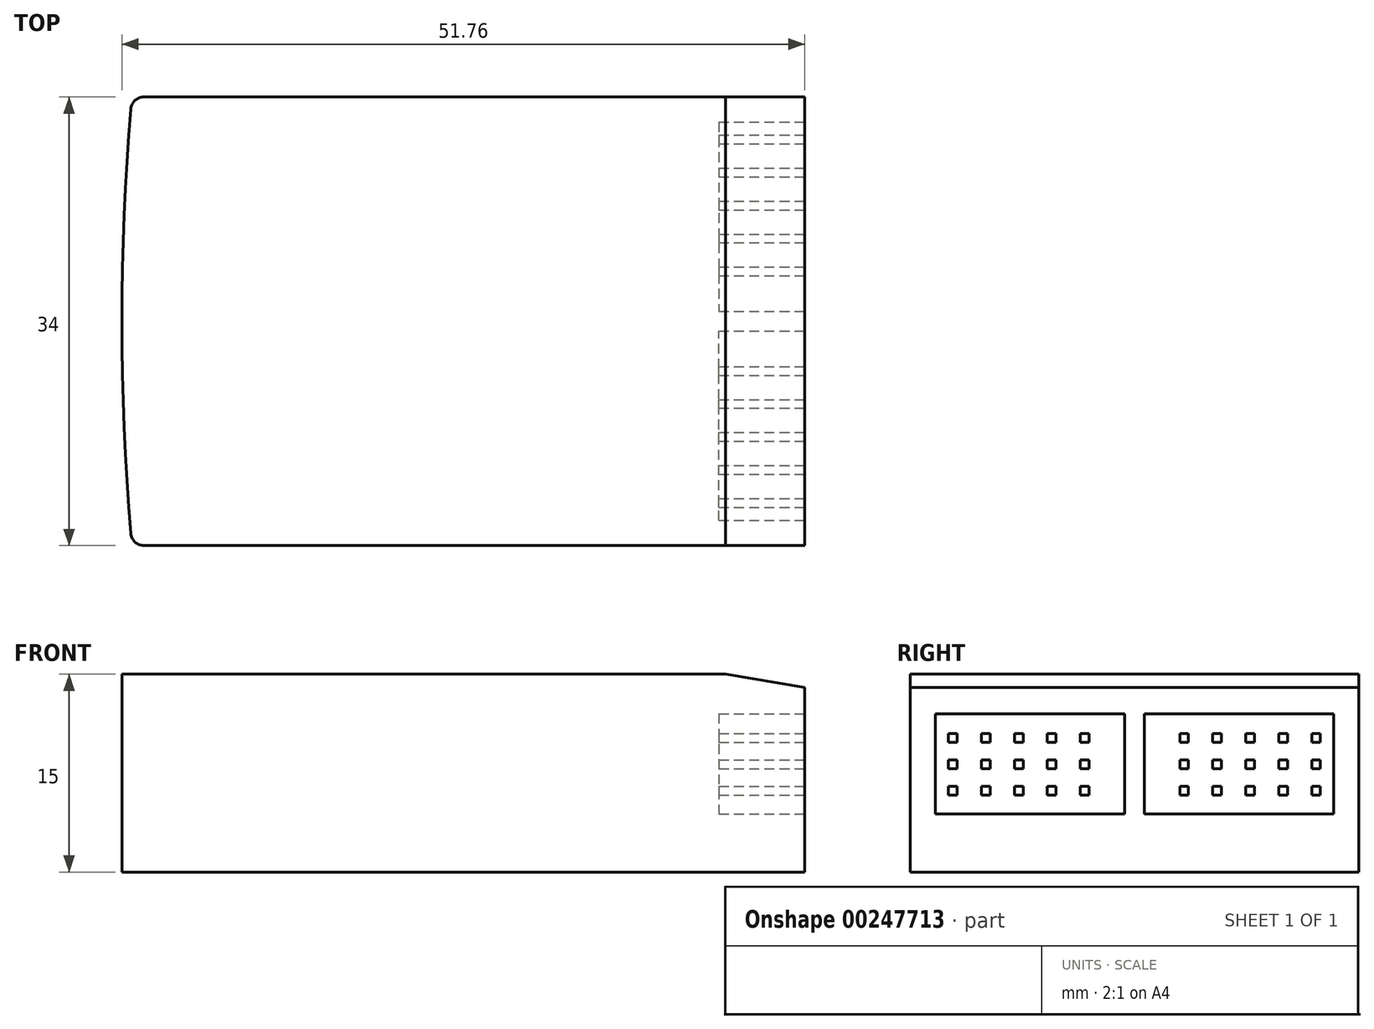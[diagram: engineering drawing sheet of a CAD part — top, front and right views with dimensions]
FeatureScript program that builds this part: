
annotation { "Feature Type Name" : "Feature", "Feature Type Description" : "" }
export const myFeature = defineFeature(function(context is Context, id is Id, definition is map)
    precondition{}
    {
        {
            var Q0;
            Q0=qCreatedBy(makeId("Top.planeOp"),FACE);
            var sketch = newSketch(context, id + "F0", { "sketchPlane" : qUnion([Q0])});
            skLineSegment(sketch, "E0.bottom", {"start": v(-8.7, 28.02) * mm, "end": v(42.3, 28.02) * mm});
            skLineSegment(sketch, "E0.top", {"start": v(-8.7, -5.98) * mm, "end": v(42.3, -5.98) * mm});
            skLineSegment(sketch, "E0.right", {"start": v(42.3, 28.02) * mm, "end": v(42.3, -5.98) * mm});
            skArc(sketch, "E1", {"start": v(-8.7, 28.02) * mm, "mid": v(-9.46, 11.02) * mm, "end": v(-8.7, -5.98) * mm});
            skSolve(sketch);
        }
        {
            var Q0;
            Q0 = qSketchRegion(id + "F0", true);
            extrude(context, id + "F1", {"entities" : qUnion([Q0]), "depth" : 15 * mm});
        }
        {
            var Q0;
            Q0=makeQuery(id+"F1.opExtrude","CAP_EDGE",EDGE,{"disambiguationData":[OSD([sQuery(id+"F0.wireOp",EDGE,"E0.right")])],"isStart":false});
            chamfer(context, id + "F2", {"entities" : qUnion([Q0]), "chamferType" : ChamferType.TWO_OFFSETS, "width1" : 1 * mm, "oppositeDirection" : false, "width2" : 6 * mm, "tangentPropagation" : true});
        }
        {
            var Q0;
            Q0=makeQuery(id+"F1.opExtrude","SWEPT_FACE",FACE,{"disambiguationData":[OSD([sQuery(id+"F0.wireOp",EDGE,"E0.right")])]});
            var sketch = newSketch(context, id + "F3", { "sketchPlane" : qUnion([Q0])});
            skLineSegment(sketch, "E2", {"start": v(11.02, 14) * mm, "end": v(11.02, 0) * mm});
            skLineSegment(sketch, "E3.bottom", {"start": v(-4.08, 12) * mm, "end": v(9.92, 12) * mm});
            skLineSegment(sketch, "E3.top", {"start": v(-4.08, 4.4) * mm, "end": v(9.92, 4.4) * mm});
            skLineSegment(sketch, "E3.left", {"start": v(-4.08, 12) * mm, "end": v(-4.08, 4.4) * mm});
            skLineSegment(sketch, "E4", {"start": v(10.27, 14) * mm, "end": v(10.27, 0) * mm});
            skLineSegment(sketch, "E5.MirrorCS", {"start": v(11.77, 14) * mm, "end": v(11.77, 0) * mm});
            skLineSegment(sketch, "E6.0", {"start": v(28.02, 14) * mm, "end": v(28.02, 0) * mm});
            skLineSegment(sketch, "E7", {"start": v(9.92, 4.4) * mm, "end": v(10.27, 4.4) * mm});
            skLineSegment(sketch, "E8", {"start": v(9.92, 12) * mm, "end": v(10.27, 12) * mm});
            skLineSegment(sketch, "E9.MirrorCS", {"start": v(12.12, 4.4) * mm, "end": v(11.77, 4.4) * mm});
            skLineSegment(sketch, "E10.MirrorCS", {"start": v(12.12, 12) * mm, "end": v(11.77, 12) * mm});
            skLineSegment(sketch, "E11.MirrorCS", {"start": v(26.12, 12) * mm, "end": v(12.12, 12) * mm});
            skLineSegment(sketch, "E12.MirrorCS", {"start": v(26.12, 12) * mm, "end": v(26.12, 4.4) * mm});
            skLineSegment(sketch, "E13.MirrorCS", {"start": v(26.12, 4.4) * mm, "end": v(12.12, 4.4) * mm});
            skLineSegment(sketch, "E14.bottom", {"start": v(-3.08, 10.5) * mm, "end": v(-2.42, 10.5) * mm});
            skLineSegment(sketch, "E14.top", {"start": v(-3.08, 9.84) * mm, "end": v(-2.42, 9.84) * mm});
            skLineSegment(sketch, "E14.left", {"start": v(-3.08, 10.5) * mm, "end": v(-3.08, 9.84) * mm});
            skLineSegment(sketch, "E14.right", {"start": v(-2.42, 10.5) * mm, "end": v(-2.42, 9.84) * mm});
            skLineSegment(sketch, "E15.0.1.0", {"start": v(-2.42, 8.5) * mm, "end": v(-2.42, 7.84) * mm});
            skLineSegment(sketch, "E15.0.1.1", {"start": v(-3.08, 8.5) * mm, "end": v(-2.42, 8.5) * mm});
            skLineSegment(sketch, "E15.0.1.2", {"start": v(-3.08, 8.5) * mm, "end": v(-3.08, 7.84) * mm});
            skLineSegment(sketch, "E15.0.1.3", {"start": v(-3.08, 7.84) * mm, "end": v(-2.42, 7.84) * mm});
            skLineSegment(sketch, "E15.0.2.0", {"start": v(-2.42, 6.5) * mm, "end": v(-2.42, 5.84) * mm});
            skLineSegment(sketch, "E15.0.2.1", {"start": v(-3.08, 6.5) * mm, "end": v(-2.42, 6.5) * mm});
            skLineSegment(sketch, "E15.0.2.2", {"start": v(-3.08, 6.5) * mm, "end": v(-3.08, 5.84) * mm});
            skLineSegment(sketch, "E15.0.2.3", {"start": v(-3.08, 5.84) * mm, "end": v(-2.42, 5.84) * mm});
            skLineSegment(sketch, "E15.1.0.0", {"start": v(0.08, 10.5) * mm, "end": v(0.08, 9.84) * mm});
            skLineSegment(sketch, "E15.1.0.1", {"start": v(-0.58, 10.5) * mm, "end": v(0.08, 10.5) * mm});
            skLineSegment(sketch, "E15.1.0.2", {"start": v(-0.58, 10.5) * mm, "end": v(-0.58, 9.84) * mm});
            skLineSegment(sketch, "E15.1.0.3", {"start": v(-0.58, 9.84) * mm, "end": v(0.08, 9.84) * mm});
            skLineSegment(sketch, "E15.1.1.0", {"start": v(0.08, 8.5) * mm, "end": v(0.08, 7.84) * mm});
            skLineSegment(sketch, "E15.1.1.1", {"start": v(-0.58, 8.5) * mm, "end": v(0.08, 8.5) * mm});
            skLineSegment(sketch, "E15.1.1.2", {"start": v(-0.58, 8.5) * mm, "end": v(-0.58, 7.84) * mm});
            skLineSegment(sketch, "E15.1.1.3", {"start": v(-0.58, 7.84) * mm, "end": v(0.08, 7.84) * mm});
            skLineSegment(sketch, "E15.1.2.0", {"start": v(0.08, 6.5) * mm, "end": v(0.08, 5.84) * mm});
            skLineSegment(sketch, "E15.1.2.1", {"start": v(-0.58, 6.5) * mm, "end": v(0.08, 6.5) * mm});
            skLineSegment(sketch, "E15.1.2.2", {"start": v(-0.58, 6.5) * mm, "end": v(-0.58, 5.84) * mm});
            skLineSegment(sketch, "E15.1.2.3", {"start": v(-0.58, 5.84) * mm, "end": v(0.08, 5.84) * mm});
            skLineSegment(sketch, "E15.2.0.0", {"start": v(2.58, 10.5) * mm, "end": v(2.58, 9.84) * mm});
            skLineSegment(sketch, "E15.2.0.1", {"start": v(1.92, 10.5) * mm, "end": v(2.58, 10.5) * mm});
            skLineSegment(sketch, "E15.2.0.2", {"start": v(1.92, 10.5) * mm, "end": v(1.92, 9.84) * mm});
            skLineSegment(sketch, "E15.2.0.3", {"start": v(1.92, 9.84) * mm, "end": v(2.58, 9.84) * mm});
            skLineSegment(sketch, "E15.2.1.0", {"start": v(2.58, 8.5) * mm, "end": v(2.58, 7.84) * mm});
            skLineSegment(sketch, "E15.2.1.1", {"start": v(1.92, 8.5) * mm, "end": v(2.58, 8.5) * mm});
            skLineSegment(sketch, "E15.2.1.2", {"start": v(1.92, 8.5) * mm, "end": v(1.92, 7.84) * mm});
            skLineSegment(sketch, "E15.2.1.3", {"start": v(1.92, 7.84) * mm, "end": v(2.58, 7.84) * mm});
            skLineSegment(sketch, "E15.2.2.0", {"start": v(2.58, 6.5) * mm, "end": v(2.58, 5.84) * mm});
            skLineSegment(sketch, "E15.2.2.1", {"start": v(1.92, 6.5) * mm, "end": v(2.58, 6.5) * mm});
            skLineSegment(sketch, "E15.2.2.2", {"start": v(1.92, 6.5) * mm, "end": v(1.92, 5.84) * mm});
            skLineSegment(sketch, "E15.2.2.3", {"start": v(1.92, 5.84) * mm, "end": v(2.58, 5.84) * mm});
            skLineSegment(sketch, "E15.3.0.0", {"start": v(5.08, 10.5) * mm, "end": v(5.08, 9.84) * mm});
            skLineSegment(sketch, "E15.3.0.1", {"start": v(4.42, 10.5) * mm, "end": v(5.08, 10.5) * mm});
            skLineSegment(sketch, "E15.3.0.2", {"start": v(4.42, 10.5) * mm, "end": v(4.42, 9.84) * mm});
            skLineSegment(sketch, "E15.3.0.3", {"start": v(4.42, 9.84) * mm, "end": v(5.08, 9.84) * mm});
            skLineSegment(sketch, "E15.3.1.0", {"start": v(5.08, 8.5) * mm, "end": v(5.08, 7.84) * mm});
            skLineSegment(sketch, "E15.3.1.1", {"start": v(4.42, 8.5) * mm, "end": v(5.08, 8.5) * mm});
            skLineSegment(sketch, "E15.3.1.2", {"start": v(4.42, 8.5) * mm, "end": v(4.42, 7.84) * mm});
            skLineSegment(sketch, "E15.3.1.3", {"start": v(4.42, 7.84) * mm, "end": v(5.08, 7.84) * mm});
            skLineSegment(sketch, "E15.3.2.0", {"start": v(5.08, 6.5) * mm, "end": v(5.08, 5.84) * mm});
            skLineSegment(sketch, "E15.3.2.1", {"start": v(4.42, 6.5) * mm, "end": v(5.08, 6.5) * mm});
            skLineSegment(sketch, "E15.3.2.2", {"start": v(4.42, 6.5) * mm, "end": v(4.42, 5.84) * mm});
            skLineSegment(sketch, "E15.3.2.3", {"start": v(4.42, 5.84) * mm, "end": v(5.08, 5.84) * mm});
            skLineSegment(sketch, "E15.4.0.0", {"start": v(7.58, 10.5) * mm, "end": v(7.58, 9.84) * mm});
            skLineSegment(sketch, "E15.4.0.1", {"start": v(6.92, 10.5) * mm, "end": v(7.58, 10.5) * mm});
            skLineSegment(sketch, "E15.4.0.2", {"start": v(6.92, 10.5) * mm, "end": v(6.92, 9.84) * mm});
            skLineSegment(sketch, "E15.4.0.3", {"start": v(6.92, 9.84) * mm, "end": v(7.58, 9.84) * mm});
            skLineSegment(sketch, "E15.4.1.0", {"start": v(7.58, 8.5) * mm, "end": v(7.58, 7.84) * mm});
            skLineSegment(sketch, "E15.4.1.1", {"start": v(6.92, 8.5) * mm, "end": v(7.58, 8.5) * mm});
            skLineSegment(sketch, "E15.4.1.2", {"start": v(6.92, 8.5) * mm, "end": v(6.92, 7.84) * mm});
            skLineSegment(sketch, "E15.4.1.3", {"start": v(6.92, 7.84) * mm, "end": v(7.58, 7.84) * mm});
            skLineSegment(sketch, "E15.4.2.0", {"start": v(7.58, 6.5) * mm, "end": v(7.58, 5.84) * mm});
            skLineSegment(sketch, "E15.4.2.1", {"start": v(6.92, 6.5) * mm, "end": v(7.58, 6.5) * mm});
            skLineSegment(sketch, "E15.4.2.2", {"start": v(6.92, 6.5) * mm, "end": v(6.92, 5.84) * mm});
            skLineSegment(sketch, "E15.4.2.3", {"start": v(6.92, 5.84) * mm, "end": v(7.58, 5.84) * mm});
            skLineSegment(sketch, "E15.direction1", {"start": v(-3.08, 9.84) * mm, "end": v(-0.58, 9.84) * mm, "construction": true});
            skLineSegment(sketch, "E15.direction2", {"start": v(-3.08, 9.84) * mm, "end": v(-3.08, 7.84) * mm, "construction": true});
            skLineSegment(sketch, "E16.MirrorCS", {"start": v(25.12, 9.84) * mm, "end": v(24.46, 9.84) * mm});
            skLineSegment(sketch, "E17.MirrorCS", {"start": v(25.12, 8.5) * mm, "end": v(25.12, 7.84) * mm});
            skLineSegment(sketch, "E18.MirrorCS", {"start": v(17.62, 6.5) * mm, "end": v(17.62, 5.84) * mm});
            skLineSegment(sketch, "E19.MirrorCS", {"start": v(20.12, 8.5) * mm, "end": v(20.12, 7.84) * mm});
            skLineSegment(sketch, "E20.MirrorCS", {"start": v(22.62, 10.5) * mm, "end": v(22.62, 9.84) * mm});
            skLineSegment(sketch, "E21.MirrorCS", {"start": v(25.12, 7.84) * mm, "end": v(24.46, 7.84) * mm});
            skLineSegment(sketch, "E22.MirrorCS", {"start": v(14.46, 10.5) * mm, "end": v(14.46, 9.84) * mm});
            skLineSegment(sketch, "E23.MirrorCS", {"start": v(15.12, 7.84) * mm, "end": v(14.46, 7.84) * mm});
            skLineSegment(sketch, "E24.MirrorCS", {"start": v(17.62, 9.84) * mm, "end": v(16.96, 9.84) * mm});
            skLineSegment(sketch, "E25.MirrorCS", {"start": v(19.46, 6.5) * mm, "end": v(19.46, 5.84) * mm});
            skLineSegment(sketch, "E26.MirrorCS", {"start": v(22.62, 5.84) * mm, "end": v(21.96, 5.84) * mm});
            skLineSegment(sketch, "E27.MirrorCS", {"start": v(21.96, 8.5) * mm, "end": v(21.96, 7.84) * mm});
            skLineSegment(sketch, "E28.MirrorCS", {"start": v(24.46, 6.5) * mm, "end": v(24.46, 5.84) * mm});
            skLineSegment(sketch, "E29.MirrorCS", {"start": v(15.12, 10.5) * mm, "end": v(14.46, 10.5) * mm});
            skLineSegment(sketch, "E30.MirrorCS", {"start": v(14.46, 6.5) * mm, "end": v(14.46, 5.84) * mm});
            skLineSegment(sketch, "E31.MirrorCS", {"start": v(16.96, 8.5) * mm, "end": v(16.96, 7.84) * mm});
            skLineSegment(sketch, "E32.MirrorCS", {"start": v(20.12, 6.5) * mm, "end": v(19.46, 6.5) * mm});
            skLineSegment(sketch, "E33.MirrorCS", {"start": v(19.46, 10.5) * mm, "end": v(19.46, 9.84) * mm});
            skLineSegment(sketch, "E34.MirrorCS", {"start": v(22.62, 8.5) * mm, "end": v(21.96, 8.5) * mm});
            skLineSegment(sketch, "E35.MirrorCS", {"start": v(15.12, 10.5) * mm, "end": v(15.12, 9.84) * mm});
            skLineSegment(sketch, "E36.MirrorCS", {"start": v(20.12, 6.5) * mm, "end": v(20.12, 5.84) * mm});
            skLineSegment(sketch, "E37.MirrorCS", {"start": v(22.62, 8.5) * mm, "end": v(22.62, 7.84) * mm});
            skLineSegment(sketch, "E38.MirrorCS", {"start": v(17.62, 8.5) * mm, "end": v(16.96, 8.5) * mm});
            skLineSegment(sketch, "E39.MirrorCS", {"start": v(20.12, 10.5) * mm, "end": v(19.46, 10.5) * mm});
            skLineSegment(sketch, "E40.MirrorCS", {"start": v(25.12, 6.5) * mm, "end": v(24.46, 6.5) * mm});
            skLineSegment(sketch, "E41.MirrorCS", {"start": v(25.12, 10.5) * mm, "end": v(25.12, 9.84) * mm});
            skLineSegment(sketch, "E42.MirrorCS", {"start": v(15.12, 6.5) * mm, "end": v(14.46, 6.5) * mm});
            skLineSegment(sketch, "E43.MirrorCS", {"start": v(17.62, 8.5) * mm, "end": v(17.62, 7.84) * mm});
            skLineSegment(sketch, "E44.MirrorCS", {"start": v(20.12, 10.5) * mm, "end": v(20.12, 9.84) * mm});
            skLineSegment(sketch, "E45.MirrorCS", {"start": v(25.12, 6.5) * mm, "end": v(25.12, 5.84) * mm});
            skLineSegment(sketch, "E46.MirrorCS", {"start": v(15.12, 6.5) * mm, "end": v(15.12, 5.84) * mm});
            skLineSegment(sketch, "E47.MirrorCS", {"start": v(24.46, 10.5) * mm, "end": v(24.46, 9.84) * mm});
            skLineSegment(sketch, "E48.MirrorCS", {"start": v(15.12, 9.84) * mm, "end": v(14.46, 9.84) * mm});
            skLineSegment(sketch, "E49.MirrorCS", {"start": v(22.62, 7.84) * mm, "end": v(21.96, 7.84) * mm});
            skLineSegment(sketch, "E50.MirrorCS", {"start": v(20.12, 5.84) * mm, "end": v(19.46, 5.84) * mm});
            skLineSegment(sketch, "E51.MirrorCS", {"start": v(17.62, 7.84) * mm, "end": v(16.96, 7.84) * mm});
            skLineSegment(sketch, "E52.MirrorCS", {"start": v(20.12, 9.84) * mm, "end": v(19.46, 9.84) * mm});
            skLineSegment(sketch, "E53.MirrorCS", {"start": v(25.12, 5.84) * mm, "end": v(24.46, 5.84) * mm});
            skLineSegment(sketch, "E54.MirrorCS", {"start": v(15.12, 5.84) * mm, "end": v(14.46, 5.84) * mm});
            skLineSegment(sketch, "E55.MirrorCS", {"start": v(25.12, 10.5) * mm, "end": v(24.46, 10.5) * mm});
            skLineSegment(sketch, "E56.MirrorCS", {"start": v(24.46, 8.5) * mm, "end": v(24.46, 7.84) * mm});
            skLineSegment(sketch, "E57.MirrorCS", {"start": v(14.46, 8.5) * mm, "end": v(14.46, 7.84) * mm});
            skLineSegment(sketch, "E58.MirrorCS", {"start": v(16.96, 10.5) * mm, "end": v(16.96, 9.84) * mm});
            skLineSegment(sketch, "E59.MirrorCS", {"start": v(21.96, 6.5) * mm, "end": v(21.96, 5.84) * mm});
            skLineSegment(sketch, "E60.MirrorCS", {"start": v(17.62, 6.5) * mm, "end": v(16.96, 6.5) * mm});
            skLineSegment(sketch, "E61.MirrorCS", {"start": v(20.12, 8.5) * mm, "end": v(19.46, 8.5) * mm});
            skLineSegment(sketch, "E62.MirrorCS", {"start": v(25.12, 9.84) * mm, "end": v(25.12, 7.84) * mm, "construction": true});
            skLineSegment(sketch, "E63.MirrorCS", {"start": v(22.62, 10.5) * mm, "end": v(21.96, 10.5) * mm});
            skLineSegment(sketch, "E64.MirrorCS", {"start": v(15.12, 8.5) * mm, "end": v(15.12, 7.84) * mm});
            skLineSegment(sketch, "E65.MirrorCS", {"start": v(17.62, 5.84) * mm, "end": v(16.96, 5.84) * mm});
            skLineSegment(sketch, "E66.MirrorCS", {"start": v(22.62, 6.5) * mm, "end": v(22.62, 5.84) * mm});
            skLineSegment(sketch, "E67.MirrorCS", {"start": v(22.62, 9.84) * mm, "end": v(21.96, 9.84) * mm});
            skLineSegment(sketch, "E68.MirrorCS", {"start": v(25.12, 8.5) * mm, "end": v(24.46, 8.5) * mm});
            skLineSegment(sketch, "E69.MirrorCS", {"start": v(20.12, 7.84) * mm, "end": v(19.46, 7.84) * mm});
            skLineSegment(sketch, "E70.MirrorCS", {"start": v(16.96, 6.5) * mm, "end": v(16.96, 5.84) * mm});
            skLineSegment(sketch, "E71.MirrorCS", {"start": v(17.62, 10.5) * mm, "end": v(17.62, 9.84) * mm});
            skLineSegment(sketch, "E72.MirrorCS", {"start": v(19.46, 8.5) * mm, "end": v(19.46, 7.84) * mm});
            skLineSegment(sketch, "E73.MirrorCS", {"start": v(15.12, 8.5) * mm, "end": v(14.46, 8.5) * mm});
            skLineSegment(sketch, "E74.MirrorCS", {"start": v(17.62, 10.5) * mm, "end": v(16.96, 10.5) * mm});
            skLineSegment(sketch, "E75.MirrorCS", {"start": v(22.62, 6.5) * mm, "end": v(21.96, 6.5) * mm});
            skLineSegment(sketch, "E76.MirrorCS", {"start": v(21.96, 10.5) * mm, "end": v(21.96, 9.84) * mm});
            skLineSegment(sketch, "E77.MirrorCS", {"start": v(25.12, 9.84) * mm, "end": v(22.62, 9.84) * mm, "construction": true});
            skSolve(sketch);
        }
        {
            var Q0;
            Q0 = qSketchRegion(id + "F3", true);
            extrude(context, id + "F4", {"entities" : qUnion([Q0]), "operationType" : NewBodyOperationType.REMOVE, "oppositeDirection" : true, "depth" : 6.5 * mm});
        }
        {
            var Q0;
            Q0=makeQuery(id+"F1.opExtrude","SWEPT_EDGE",EDGE,{"disambiguationData":[OSD([sQuery(id+"F0.wireOp",EDGE,"E0.top"),sQuery(id+"F0.wireOp",EDGE,"E1")])]});
            var Q1;
            Q1=makeQuery(id+"F1.opExtrude","SWEPT_EDGE",EDGE,{"disambiguationData":[OSD([sQuery(id+"F0.wireOp",EDGE,"E0.bottom"),sQuery(id+"F0.wireOp",EDGE,"E1")])]});
            fillet(context, id + "F5", {"entities" : qUnion([Q0, Q1]), "radius" : 1 * mm, "tangentPropagation" : true, "allowEdgeOverflow" : false});
        }
    });
